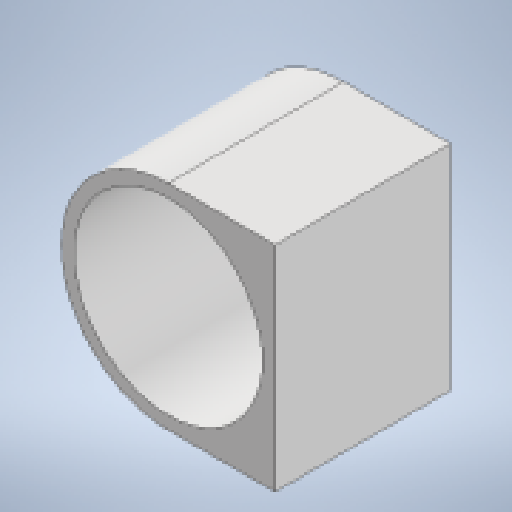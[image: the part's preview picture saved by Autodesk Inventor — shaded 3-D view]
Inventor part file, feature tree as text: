
AUTODESK INVENTOR PART (.ipt)
format: ipt  version: 2023 (Build 270158000, 158)  size: 168,448 bytes
history: native  units: mm
features: extrude x3, sketch x3, projected_geometry x2, other x1
ambient origin geometry x8: Origin, YZ Plane, XZ Plane, XY Plane, X Axis, Y Axis, Z Axis, Center Point
bodies: Body1 (feature_tree)
feature tree (9):
  other  "實體1"
  extrude  "擠出1"  Depth=50.0mm
  extrude  "擠出2"  Depth=100.0mm
  extrude  "擠出3"  Depth=3.0mm TaperAngle=0.0deg
  sketch  "草圖1"
  sketch  "草圖2"
  projected_geometry  "投影迴路1"
  sketch  "草圖3"
  projected_geometry  "投影迴路2"
